# Revit family: _Camera-Security-Panasonic-Super_Dynamic-Weatherproof-Network-S1572LSeries
name_source: partatom
category: 警備装置
units: mm (PartAtom-declared; Revit-internal decimal feet)

## family parameters
OmniClass タイトル = Cameras
OmniClass 番号 = 23.85.10.14.11
パーツ タイプ = 標準
ホスト = 面
ロード時にボイドで切り取り = いいえ
丸型コネクタ寸法 = 直径を使用
共有 = いいえ
注釈の向きを維持 = いいえ
部屋計算ポイント = いいえ

## types (2) — shared parameters
4K = Resolution : 4K
Alarm Input Or Output Specification = ALARM IN 1(Alarm input 1/ Black & white input/ Auto time adjustment input) (x1), ALARM IN 2 (Alarm input 2/ ALARM OUT) (x1), ALARM IN 3 (Alarm input 3/ AUX OUT) (x1)
Angle Of View = 104
Aspect169 = はい
Audio In = Yes
Audio Out = Yes
Communication Ports = 10Base-T / 100Base-TX, RJ45 connector
Day Or Night = Yes
Equipment Abbreviation = SC
Family Version = 1.0.0
Full HD = Resolution : Full HD
HFOV Max 169 = 104.00°
HFOV Max 43 = 104.00°
HFOV Min 169 = 53.00°
HFOV Min 43 = 53.00°
Has POE = はい
IP Or Analog = IP
Indoor Or Outdoor = Outdoor
Minimum Illumination = 0.090 lx
Model Disclaimer = Contact Panasonic for more information
Mounting Positions = Mount Dependent or Surface Mount
Operational Humidity = 10 to 100 % (no condensation)
Operational Temperature = -40 °F to 140 °F
Panning Range = -180 to +180
Power Active = 10.0 W
Product Material = Paint - Panasonic - Silver
Product Page URL = https://security.panasonic.com
Provide Feedback = https://www.surveymonkey.com
Regulatory Compliance = UL (UL60950-1), c-UL (CSA C22.2 No.60950-1), CE, IEC60950-1, FCC (Part15 ClassA), ICES003 ClassA, EN55032 ClassB, EN55024
Shock Resistance = IK10 (IEC 62262)
Storage Temperature = -40 °F to 140 °F
Super Dynamic Range = はい
Tilting Range = -100 to +100
URL = http://security.panasonic.com
VFOV Max 169 = 56.00°
VFOV Max 43 = 56.00°
VFOV Min 169 = 30.00°
VFOV Min 43 = 30.00°
Vandal Resistant = はい
Voltage DC = 12 V
WQHD = Resolution : WQHD
Water and Dust Resistance = IP66 (IEC60529), Type 4X (UL50E), NEMA 4X compliant
Width = 5.23622 "
Yaw Max = 100.00°
Yaw Min = -190.00°
Yawing Range = -190 to +100
z Base Square = はい
z Camera Center Offset = 0.2874 "
z Camera Center Offset Base = 1.1811 "
z Column Height = 3.11024 "
z Const CameraYawAxis = 15.74803 "
z Const Pan Handle Length = 27.55906 "
z Const Tilt Base Length = 9.84252 "
z Const Tilt Base2 Length = 19.68504 "
z Const Tilt Handle Length = 14.17323 "
z Const Yaw Axis Length = 7.87402 "
z Const Yaw Base Length = 10.23622 "
z Const Yaw Base2 Length = 17.32283 "
z Const Yaw Handle Length = 9.25197 "
z Hinge Height = 3.79921 "
z VV Viewpoint Depth Max = 8.2726 "
z VV Viewpoint Depth Min = 8.2726 "
製造元 = Panasonic
zero-valued in all types: 既定の高さ

## per-type parameters (varying)
| type | Date Last Modified | Part Description | Product Documentation Link | 説明 |
| WV-S1570L | 2019/05/14 | Security Camera, Super Dynamic, 4K, Weatherproof, Network, WV-S1570L | https://bizpartner.panasonic.net | Security Camera, Super Dynamic, 4K, Weatherproof, Network, WV-S1570L |
| WV-S1572L | 2020/10/13 | Security Camera, Super Dynamic, 4K, Weatherproof, Network, WV-S1572L | https://bizpartner.panasonic.net
https://bizpartner.panasonic.net | Security Camera, Super Dynamic, 4K, Weatherproof, Network, WV-S1572L |

note: column(s) folded — value = type name in every type: Part Number, モデル

## geometry (parser evidence)
native form markers: Sweep x9
no freeform markers — native parametric forms only
